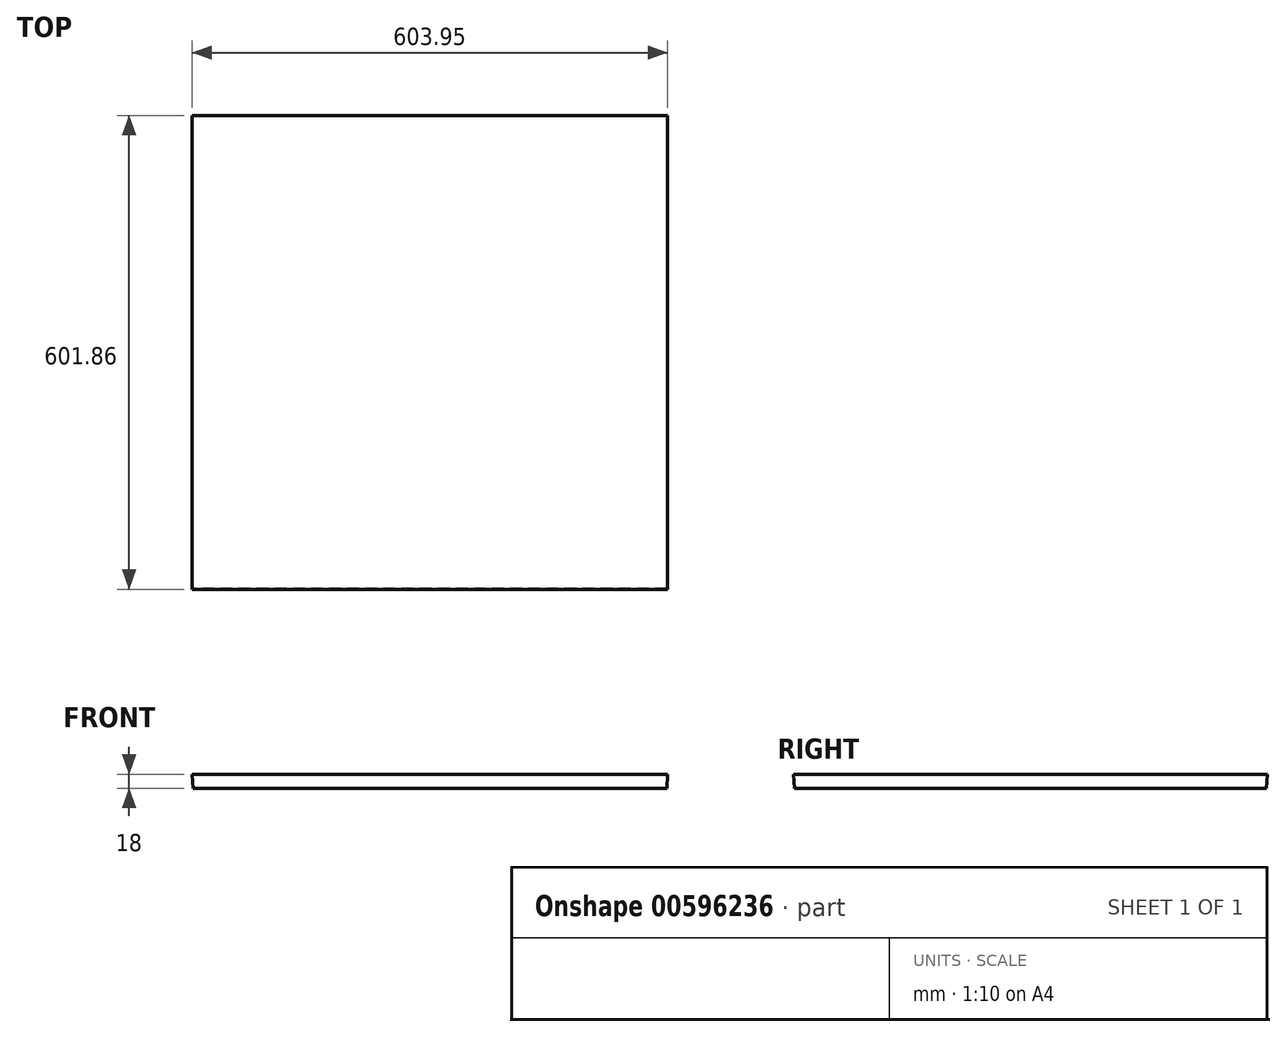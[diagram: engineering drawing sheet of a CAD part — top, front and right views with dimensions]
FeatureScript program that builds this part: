
annotation { "Feature Type Name" : "Feature", "Feature Type Description" : "" }
export const myFeature = defineFeature(function(context is Context, id is Id, definition is map)
    precondition{}
    {
        {
            var Q0;
            Q0=qCreatedBy(makeId("Top.planeOp"),FACE);
            var sketch = newSketch(context, id + "F0", { "sketchPlane" : qUnion([Q0])});
            skLineSegment(sketch, "E0.bottom", {"start": v(0, 0) * mm, "end": v(602.07, 0) * mm});
            skLineSegment(sketch, "E0.top", {"start": v(0, -599.98) * mm, "end": v(602.07, -599.98) * mm});
            skLineSegment(sketch, "E0.left", {"start": v(0, 0) * mm, "end": v(0, -599.98) * mm});
            skLineSegment(sketch, "E0.right", {"start": v(602.07, 0) * mm, "end": v(602.07, -599.98) * mm});
            skPoint(sketch, "E1.firstSnap0", {"position": v(301.04, 0) * mm});
            skSolve(sketch);
        }
        {
            var Q0;
            Q0=makeQuery(id+"F0.imprint","IMPRINT",FACE,{"disambiguationData":[TD([[makeQuery(id+"F0.imprint","IMPRINT",EDGE,{"derivedFrom":sQuery(id+"F0.wireOp",EDGE,"E0.bottom")}),-1.0]])]});
            extrude(context, id + "F1", {"entities" : qUnion([Q0]), "depth" : 18 * mm, "offsetDistance" : 25 * mm, "hasDraft" : true, "draftAngle" : 3 * degree});
        }
    });
